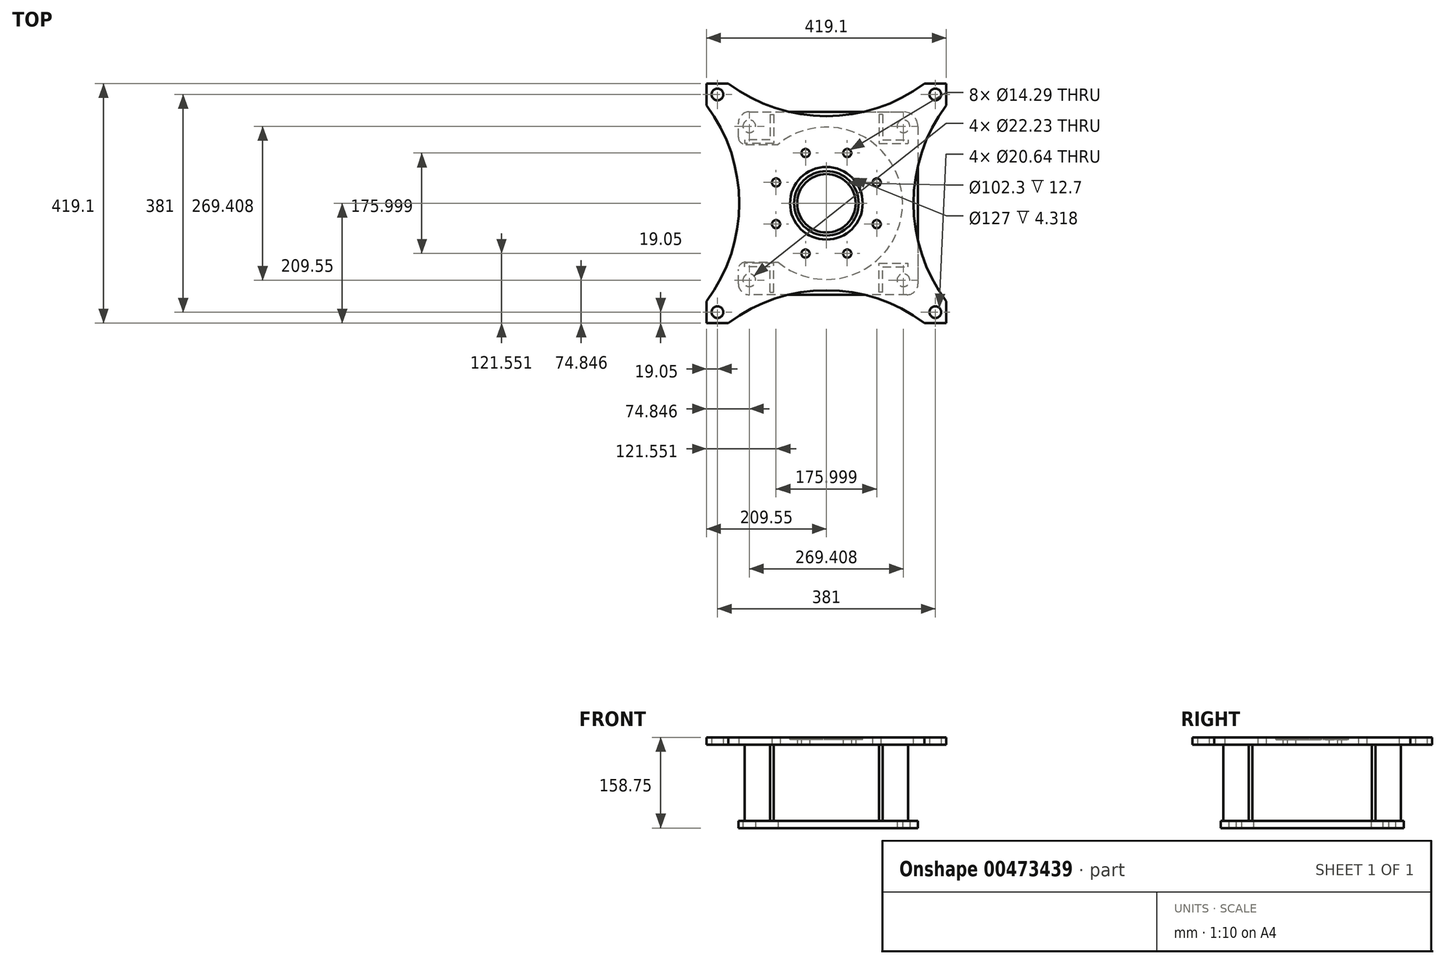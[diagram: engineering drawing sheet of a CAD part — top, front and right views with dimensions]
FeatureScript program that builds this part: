
annotation { "Feature Type Name" : "Feature", "Feature Type Description" : "" }
export const myFeature = defineFeature(function(context is Context, id is Id, definition is map)
    precondition{}
    {
        {
            var Q0;
            Q0=qCreatedBy(makeId("Top.planeOp"),FACE);
            var sketch = newSketch(context, id + "F0", { "sketchPlane" : qUnion([Q0])});
            skArc(sketch, "E0", {"start": v(-84.75, -102.95) * mm, "mid": v(133.35, 0) * mm, "end": v(-84.75, 102.95) * mm});
            skCircle(sketch, "E1", {"center": v(0, 0) * mm, "radius": 190.5 * mm, "construction": true});
            skLineSegment(sketch, "E2.0", {"start": v(-134.7, -134.7) * mm, "end": v(-134.7, 134.7) * mm, "construction": true});
            skLineSegment(sketch, "E2.1", {"start": v(-134.7, 134.7) * mm, "end": v(134.7, 134.7) * mm, "construction": true});
            skLineSegment(sketch, "E2.2", {"start": v(134.7, 134.7) * mm, "end": v(134.7, -134.7) * mm, "construction": true});
            skLineSegment(sketch, "E2.3", {"start": v(134.7, -134.7) * mm, "end": v(-134.7, -134.7) * mm, "construction": true});
            skCircle(sketch, "E3", {"center": v(-134.7, 134.7) * mm, "radius": 11.11 * mm});
            skCircle(sketch, "E4", {"center": v(134.7, 134.7) * mm, "radius": 11.11 * mm});
            skCircle(sketch, "E5", {"center": v(-134.7, -134.7) * mm, "radius": 11.11 * mm});
            skCircle(sketch, "E6", {"center": v(134.7, -134.7) * mm, "radius": 11.11 * mm});
            skLineSegment(sketch, "E7.0", {"start": v(141.05, -160.1) * mm, "end": v(-134.7, -160.1) * mm});
            skLineSegment(sketch, "E7.1", {"start": v(160.1, 134.7) * mm, "end": v(160.1, -141.05) * mm});
            skLineSegment(sketch, "E7.2", {"start": v(-134.7, 160.1) * mm, "end": v(134.7, 160.1) * mm});
            skLineSegment(sketch, "E8", {"start": v(-141.05, 102.95) * mm, "end": v(-84.75, 102.95) * mm});
            skLineSegment(sketch, "E9", {"start": v(-141.05, -102.95) * mm, "end": v(-84.75, -102.95) * mm});
            skPoint(sketch, "E10.visualSharp", {"position": v(160.1, 160.1) * mm});
            skArc(sketch, "E10.filletArc", {"start": v(160.1, 134.7) * mm, "mid": v(152.66, 152.66) * mm, "end": v(134.7, 160.1) * mm});
            skPoint(sketch, "E11.visualSharp", {"position": v(160.1, -160.1) * mm});
            skArc(sketch, "E11.filletArc", {"start": v(141.05, -160.1) * mm, "mid": v(154.52, -154.52) * mm, "end": v(160.1, -141.05) * mm});
            skLineSegment(sketch, "E12", {"start": v(-153.75, 115.65) * mm, "end": v(-153.75, 141.05) * mm});
            skPoint(sketch, "E13.visualSharp", {"position": v(-153.75, 160.1) * mm});
            skArc(sketch, "E13.filletArc", {"start": v(-134.7, 160.1) * mm, "mid": v(-148.17, 154.52) * mm, "end": v(-153.75, 141.05) * mm});
            skPoint(sketch, "E14.visualSharp", {"position": v(-153.75, 102.95) * mm});
            skArc(sketch, "E14.filletArc", {"start": v(-153.75, 115.65) * mm, "mid": v(-150.03, 106.67) * mm, "end": v(-141.05, 102.95) * mm});
            skLineSegment(sketch, "E15", {"start": v(-153.75, -141.05) * mm, "end": v(-153.75, -115.65) * mm});
            skPoint(sketch, "E16.visualSharp", {"position": v(-153.75, -102.95) * mm});
            skArc(sketch, "E16.filletArc", {"start": v(-141.05, -102.95) * mm, "mid": v(-150.03, -106.67) * mm, "end": v(-153.75, -115.65) * mm});
            skPoint(sketch, "E17.visualSharp", {"position": v(-153.75, -160.1) * mm});
            skArc(sketch, "E17.filletArc", {"start": v(-153.75, -141.05) * mm, "mid": v(-148.17, -154.52) * mm, "end": v(-134.7, -160.1) * mm});
            skSolve(sketch);
        }
        {
            var Q0;
            Q0=makeQuery(id+"F0.imprint","IMPRINT",FACE,{"disambiguationData":[TD([[makeQuery(id+"F0.imprint","IMPRINT",EDGE,{"derivedFrom":sQuery(id+"F0.wireOp",EDGE,"E0")}),-1.0]])]});
            extrude(context, id + "F1", {"entities" : qUnion([Q0]), "depth" : 12.7 * mm});
        }
        {
            var Q0;
            Q0=makeQuery(id+"F1.opExtrude","CAP_FACE",FACE,{"disambiguationData":[OSD([sQuery(id+"F0.wireOp",EDGE,"E0"),sQuery(id+"F0.wireOp",EDGE,"E3"),sQuery(id+"F0.wireOp",EDGE,"E4"),sQuery(id+"F0.wireOp",EDGE,"E5"),sQuery(id+"F0.wireOp",EDGE,"E6"),sQuery(id+"F0.wireOp",EDGE,"E7.0"),sQuery(id+"F0.wireOp",EDGE,"E7.1"),sQuery(id+"F0.wireOp",EDGE,"E7.2"),sQuery(id+"F0.wireOp",EDGE,"E8"),sQuery(id+"F0.wireOp",EDGE,"E9"),sQuery(id+"F0.wireOp",EDGE,"HDc8ByKa-qlZJ-3WXB-Y3Yh-znWmjKlYlnpf"),sQuery(id+"F0.wireOp",EDGE,"HllOg5pU-3MWT-JRd7-SyO8-p7zKC7ekhdlJ"),sQuery(id+"F0.wireOp",EDGE,"E10.filletArc"),sQuery(id+"F0.wireOp",EDGE,"E11.filletArc")])],"isStart":false});
            var sketch = newSketch(context, id + "F2", { "sketchPlane" : qUnion([Q0])});
            skLineSegment(sketch, "E18", {"start": v(-91.84, 155.34) * mm, "end": v(-91.84, 104.54) * mm});
            skLineSegment(sketch, "E19", {"start": v(-91.84, 104.54) * mm, "end": v(-142.64, 104.54) * mm});
            skLineSegment(sketch, "E20.0", {"start": v(-98.2, 110.9) * mm, "end": v(-142.64, 110.9) * mm});
            skLineSegment(sketch, "E20.1", {"start": v(-98.2, 155.34) * mm, "end": v(-98.2, 110.9) * mm});
            skLineSegment(sketch, "E21", {"start": v(-98.2, 155.34) * mm, "end": v(-91.84, 155.34) * mm});
            skLineSegment(sketch, "E22", {"start": v(-142.64, 110.9) * mm, "end": v(-142.64, 104.54) * mm});
            skSolve(sketch);
        }
        {
            var Q0;
            Q0=makeQuery(id+"F2.imprint","IMPRINT",FACE,{"disambiguationData":[TD([[makeQuery(id+"F2.imprint","IMPRINT",EDGE,{"derivedFrom":sQuery(id+"F2.wireOp",EDGE,"E18")}),-1.0]])]});
            extrude(context, id + "F3", {"entities" : qUnion([Q0]), "depth" : 133.35 * mm});
        }
        {
            var Q0;
            Q0=makeQuery(id+"F3.opExtrude","SWEPT_BODY",BODY,{"disambiguationData":[OSD([sQuery(id+"F2.wireOp",EDGE,"E18"),sQuery(id+"F2.wireOp",EDGE,"E19"),sQuery(id+"F2.wireOp",EDGE,"E20.0"),sQuery(id+"F2.wireOp",EDGE,"E20.1"),sQuery(id+"F2.wireOp",EDGE,"E21"),sQuery(id+"F2.wireOp",EDGE,"E22")])]});
            var Q1;
            Q1=qCreatedBy(makeId("Right.planeOp"),FACE);
            mirror(context, id + "F4", {"entities" : qUnion([Q0]), "mirrorPlane" : qUnion([Q1])});
        }
        {
            var Q0;
            Q0=makeQuery(id+"F3.opExtrude","SWEPT_BODY",BODY,{"disambiguationData":[OSD([sQuery(id+"F2.wireOp",EDGE,"E18"),sQuery(id+"F2.wireOp",EDGE,"E19"),sQuery(id+"F2.wireOp",EDGE,"E20.0"),sQuery(id+"F2.wireOp",EDGE,"E20.1"),sQuery(id+"F2.wireOp",EDGE,"E21"),sQuery(id+"F2.wireOp",EDGE,"E22")])]});
            var Q1;
            Q1=makeQuery(id+"F4.opPattern","COPY",BODY,{"derivedFrom":makeQuery(id+"F3.opExtrude","SWEPT_BODY",BODY,{"disambiguationData":[OSD([sQuery(id+"F2.wireOp",EDGE,"E18"),sQuery(id+"F2.wireOp",EDGE,"E19"),sQuery(id+"F2.wireOp",EDGE,"E20.0"),sQuery(id+"F2.wireOp",EDGE,"E20.1"),sQuery(id+"F2.wireOp",EDGE,"E21"),sQuery(id+"F2.wireOp",EDGE,"E22")])]}),"instanceName":"1"});
            var Q2;
            Q2=qCreatedBy(makeId("Front.planeOp"),FACE);
            mirror(context, id + "F5", {"entities" : qUnion([Q0, Q1]), "mirrorPlane" : qUnion([Q2])});
        }
        {
            var Q0;
            Q0=makeQuery(id+"F3.opExtrude","CAP_FACE",FACE,{"disambiguationData":[OSD([sQuery(id+"F2.wireOp",EDGE,"E18"),sQuery(id+"F2.wireOp",EDGE,"E19"),sQuery(id+"F2.wireOp",EDGE,"E20.0"),sQuery(id+"F2.wireOp",EDGE,"E20.1"),sQuery(id+"F2.wireOp",EDGE,"E21"),sQuery(id+"F2.wireOp",EDGE,"E22")])],"isStart":false});
            var sketch = newSketch(context, id + "F6", { "sketchPlane" : qUnion([Q0])});
            skArc(sketch, "E23.0", {"start": v(-84.75, -102.95) * mm, "mid": v(133.35, 0) * mm, "end": v(-84.75, 102.95) * mm, "construction": true});
            skCircle(sketch, "E24", {"center": v(0, 0) * mm, "radius": 133.35 * mm, "construction": true});
            skLineSegment(sketch, "E25.bottom", {"start": v(190.5, 190.5) * mm, "end": v(-190.5, 190.5) * mm, "construction": true});
            skLineSegment(sketch, "E25.top", {"start": v(190.5, -190.5) * mm, "end": v(-190.5, -190.5) * mm, "construction": true});
            skLineSegment(sketch, "E25.left", {"start": v(190.5, 190.5) * mm, "end": v(190.5, -190.5) * mm, "construction": true});
            skLineSegment(sketch, "E25.right", {"start": v(-190.5, 190.5) * mm, "end": v(-190.5, -190.5) * mm, "construction": true});
            skLineSegment(sketch, "E26.bottom", {"start": v(209.55, 209.55) * mm, "end": v(-209.55, 209.55) * mm});
            skLineSegment(sketch, "E26.top", {"start": v(209.55, -209.55) * mm, "end": v(-209.55, -209.55) * mm});
            skLineSegment(sketch, "E26.left", {"start": v(209.55, 209.55) * mm, "end": v(209.55, -209.55) * mm});
            skLineSegment(sketch, "E26.right", {"start": v(-209.55, 209.55) * mm, "end": v(-209.55, -209.55) * mm});
            skCircle(sketch, "E27", {"center": v(-190.5, 190.5) * mm, "radius": 10.32 * mm});
            skCircle(sketch, "E28.MirrorC", {"center": v(190.5, 190.5) * mm, "radius": 10.32 * mm});
            skCircle(sketch, "E29.MirrorC", {"center": v(-190.5, -190.5) * mm, "radius": 10.32 * mm});
            skCircle(sketch, "E30.MirrorC", {"center": v(190.5, -190.5) * mm, "radius": 10.32 * mm});
            skCircle(sketch, "E31", {"center": v(0, 0) * mm, "radius": 51.15 * mm});
            skCircle(sketch, "E32", {"center": v(0, 0) * mm, "radius": 95.25 * mm, "construction": true});
            skCircle(sketch, "E33", {"center": v(36.45, 88) * mm, "radius": 7.14 * mm});
            skCircle(sketch, "E34.1.0", {"center": v(-36.45, 88) * mm, "radius": 7.14 * mm});
            skCircle(sketch, "E34.2.0", {"center": v(-88, 36.45) * mm, "radius": 7.14 * mm});
            skCircle(sketch, "E34.3.0", {"center": v(-88, -36.45) * mm, "radius": 7.14 * mm});
            skCircle(sketch, "E34.4.0", {"center": v(-36.45, -88) * mm, "radius": 7.14 * mm});
            skCircle(sketch, "E34.5.0", {"center": v(36.45, -88) * mm, "radius": 7.14 * mm});
            skCircle(sketch, "E34.6.0", {"center": v(88, -36.45) * mm, "radius": 7.14 * mm});
            skCircle(sketch, "E34.7.0", {"center": v(88, 36.45) * mm, "radius": 7.14 * mm});
            skLineSegment(sketch, "E35", {"start": v(-36.45, 88) * mm, "end": v(36.45, 88) * mm, "construction": true});
            skSolve(sketch);
        }
        {
            var Q0;
            Q0=makeQuery(id+"F6.imprint","IMPRINT",FACE,{"disambiguationData":[TD([[makeQuery(id+"F6.imprint","IMPRINT",EDGE,{"derivedFrom":sQuery(id+"F6.wireOp",EDGE,"E24")}),-1.0]])]});
            var Q1;
            Q1=makeQuery(id+"F6.imprint","IMPRINT",FACE,{"disambiguationData":[TD([[makeQuery(id+"F6.imprint","IMPRINT",EDGE,{"derivedFrom":sQuery(id+"F6.wireOp",EDGE,"E26.bottom")}),1.0]])]});
            var Q2;
            Q2=makeQuery(id+"F6.imprint","IMPRINT",FACE,{"disambiguationData":[TD([[makeQuery(id+"F6.imprint","IMPRINT",EDGE,{"derivedFrom":makeQuery(id+"F3.opExtrude","CAP_EDGE",EDGE,{"disambiguationData":[OSD([sQuery(id+"F2.wireOp",EDGE,"E18")])],"isStart":false})}),-1.0]])]});
            extrude(context, id + "F7", {"entities" : qUnion([Q0, Q1, Q2]), "depth" : 12.7 * mm});
        }
        {
            var Q0;
            Q0=makeQuery(id+"F7.opExtrude","CAP_FACE",FACE,{"disambiguationData":[OSD([sQuery(id+"F6.wireOp",EDGE,"E26.bottom"),sQuery(id+"F6.wireOp",EDGE,"E26.top"),sQuery(id+"F6.wireOp",EDGE,"E26.left"),sQuery(id+"F6.wireOp",EDGE,"E26.right"),sQuery(id+"F6.wireOp",EDGE,"E27"),sQuery(id+"F6.wireOp",EDGE,"E28.MirrorC"),sQuery(id+"F6.wireOp",EDGE,"E29.MirrorC"),sQuery(id+"F6.wireOp",EDGE,"E30.MirrorC"),sQuery(id+"F6.wireOp",EDGE,"E31"),sQuery(id+"F6.wireOp",EDGE,"E33"),sQuery(id+"F6.wireOp",EDGE,"E34.1.0"),sQuery(id+"F6.wireOp",EDGE,"E34.2.0"),sQuery(id+"F6.wireOp",EDGE,"E34.3.0"),sQuery(id+"F6.wireOp",EDGE,"E34.4.0"),sQuery(id+"F6.wireOp",EDGE,"E34.5.0"),sQuery(id+"F6.wireOp",EDGE,"E34.6.0"),sQuery(id+"F6.wireOp",EDGE,"E34.7.0")])],"isStart":false});
            var sketch = newSketch(context, id + "F8", { "sketchPlane" : qUnion([Q0])});
            skArc(sketch, "E36", {"start": v(-209.55, -171.45) * mm, "mid": v(-152.4, 0) * mm, "end": v(-209.55, 171.45) * mm});
            skLineSegment(sketch, "E37", {"start": v(-209.55, 171.45) * mm, "end": v(-209.55, -171.45) * mm});
            skArc(sketch, "E38.1.0", {"start": v(171.45, -209.55) * mm, "mid": v(0, -152.4) * mm, "end": v(-171.45, -209.55) * mm});
            skLineSegment(sketch, "E38.1.1", {"start": v(-171.45, -209.55) * mm, "end": v(171.45, -209.55) * mm});
            skArc(sketch, "E38.2.0", {"start": v(209.55, 171.45) * mm, "mid": v(152.4, 0) * mm, "end": v(209.55, -171.45) * mm});
            skLineSegment(sketch, "E38.2.1", {"start": v(209.55, -171.45) * mm, "end": v(209.55, 171.45) * mm});
            skArc(sketch, "E38.3.0", {"start": v(-171.45, 209.55) * mm, "mid": v(0, 152.4) * mm, "end": v(171.45, 209.55) * mm});
            skLineSegment(sketch, "E38.3.1", {"start": v(171.45, 209.55) * mm, "end": v(-171.45, 209.55) * mm});
            skPoint(sketch, "E38.center", {"position": v(0, 0) * mm});
            skSolve(sketch);
        }
        {
            var Q0;
            Q0=makeQuery(id+"F8.imprint","IMPRINT",FACE,{"disambiguationData":[TD([[makeQuery(id+"F8.imprint","IMPRINT",EDGE,{"derivedFrom":sQuery(id+"F8.wireOp",EDGE,"E36")}),1.0]])]});
            var Q1;
            Q1=makeQuery(id+"F8.imprint","IMPRINT",FACE,{"disambiguationData":[TD([[makeQuery(id+"F8.imprint","IMPRINT",EDGE,{"derivedFrom":sQuery(id+"F8.wireOp",EDGE,"E38.3.0")}),1.0]])]});
            var Q2;
            Q2=makeQuery(id+"F8.imprint","IMPRINT",FACE,{"disambiguationData":[TD([[makeQuery(id+"F8.imprint","IMPRINT",EDGE,{"derivedFrom":sQuery(id+"F8.wireOp",EDGE,"E38.2.0")}),1.0]])]});
            var Q3;
            Q3=makeQuery(id+"F8.imprint","IMPRINT",FACE,{"disambiguationData":[TD([[makeQuery(id+"F8.imprint","IMPRINT",EDGE,{"derivedFrom":sQuery(id+"F8.wireOp",EDGE,"E38.1.0")}),1.0]])]});
            extrude(context, id + "F9", {"entities" : qUnion([Q0, Q1, Q2, Q3]), "operationType" : NewBodyOperationType.REMOVE, "oppositeDirection" : true, "depth" : 25.4 * mm});
        }
        {
            var Q0;
            Q0=makeQuery(id+"F7.opExtrude","CAP_FACE",FACE,{"disambiguationData":[OSD([sQuery(id+"F6.wireOp",EDGE,"E26.bottom"),sQuery(id+"F6.wireOp",EDGE,"E26.top"),sQuery(id+"F6.wireOp",EDGE,"E26.left"),sQuery(id+"F6.wireOp",EDGE,"E26.right"),sQuery(id+"F6.wireOp",EDGE,"E27"),sQuery(id+"F6.wireOp",EDGE,"E28.MirrorC"),sQuery(id+"F6.wireOp",EDGE,"E29.MirrorC"),sQuery(id+"F6.wireOp",EDGE,"E30.MirrorC"),sQuery(id+"F6.wireOp",EDGE,"E31"),sQuery(id+"F6.wireOp",EDGE,"E33"),sQuery(id+"F6.wireOp",EDGE,"E34.1.0"),sQuery(id+"F6.wireOp",EDGE,"E34.2.0"),sQuery(id+"F6.wireOp",EDGE,"E34.3.0"),sQuery(id+"F6.wireOp",EDGE,"E34.4.0"),sQuery(id+"F6.wireOp",EDGE,"E34.5.0"),sQuery(id+"F6.wireOp",EDGE,"E34.6.0"),sQuery(id+"F6.wireOp",EDGE,"E34.7.0")])],"isStart":false});
            var sketch = newSketch(context, id + "F10", { "sketchPlane" : qUnion([Q0])});
            skCircle(sketch, "E39", {"center": v(0, 0) * mm, "radius": 63.5 * mm});
            skCircle(sketch, "E40.0", {"center": v(0, 0) * mm, "radius": 56.36 * mm});
            skSolve(sketch);
        }
        {
            var Q0;
            Q0=makeQuery(id+"F10.imprint","IMPRINT",FACE,{"disambiguationData":[TD([[makeQuery(id+"F10.imprint","IMPRINT",EDGE,{"derivedFrom":sQuery(id+"F10.wireOp",EDGE,"E39")}),1.0]])]});
            extrude(context, id + "F11", {"entities" : qUnion([Q0]), "operationType" : NewBodyOperationType.REMOVE, "oppositeDirection" : true, "depth" : 4.32 * mm});
        }
    });
